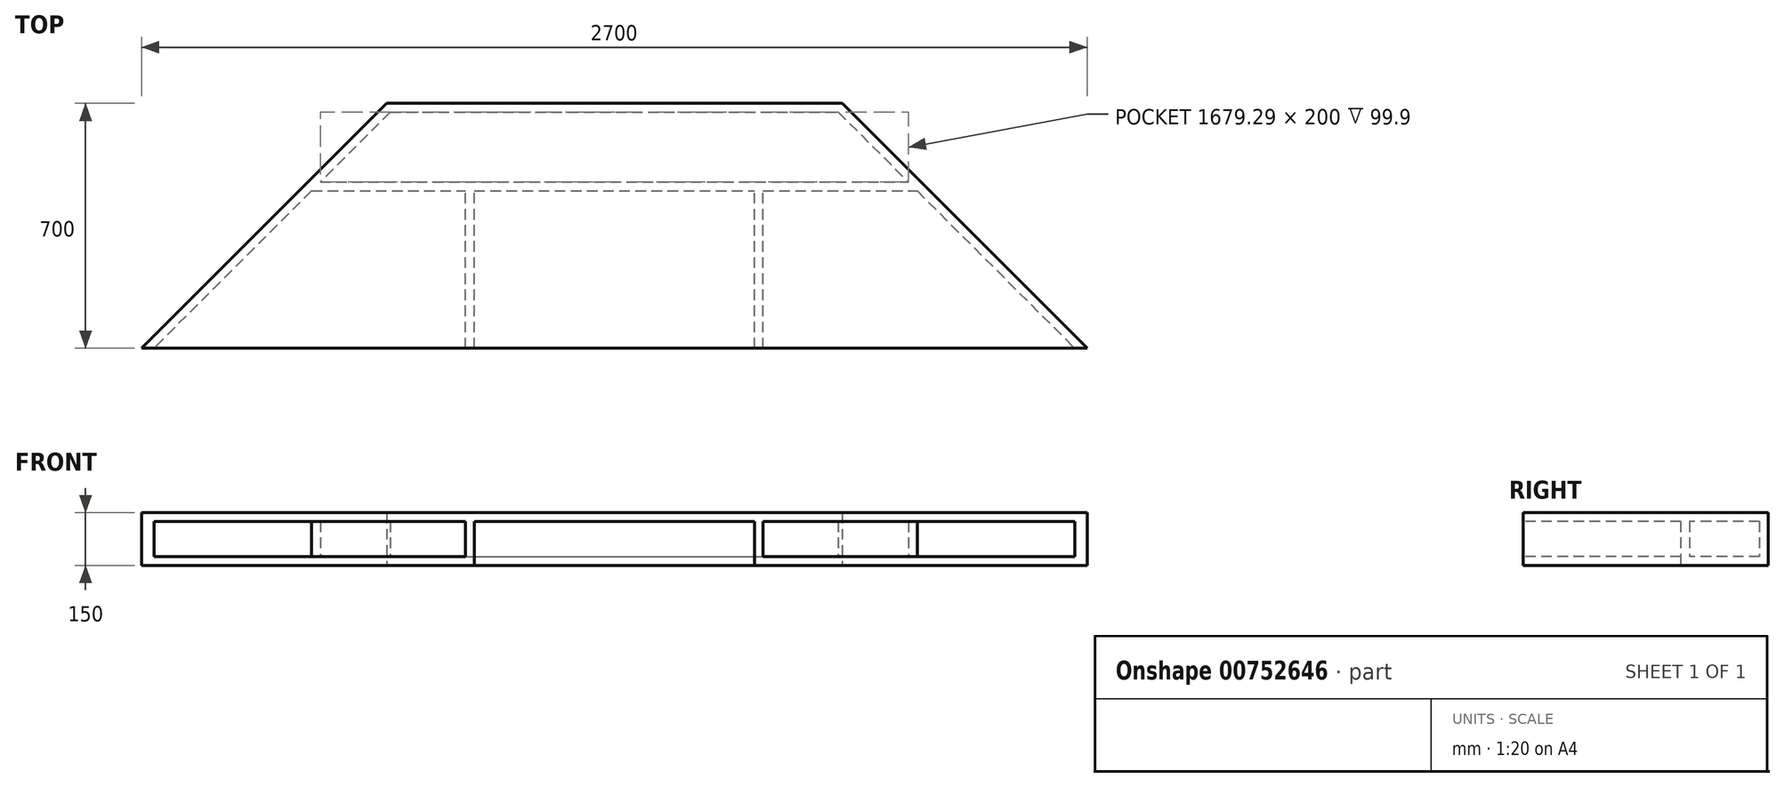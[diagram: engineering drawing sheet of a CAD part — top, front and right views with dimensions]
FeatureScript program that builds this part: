
annotation { "Feature Type Name" : "Feature", "Feature Type Description" : "" }
export const myFeature = defineFeature(function(context is Context, id is Id, definition is map)
    precondition{}
    {
        {
            var Q0;
            Q0=qCreatedBy(makeId("Top.planeOp"),FACE);
            var sketch = newSketch(context, id + "F0", { "sketchPlane" : qUnion([Q0])});
            skLineSegment(sketch, "E0", {"start": v(-650, 0) * mm, "end": v(650, 0) * mm});
            skLineSegment(sketch, "E1", {"start": v(0, 0) * mm, "end": v(0, -700) * mm});
            skLineSegment(sketch, "E2", {"start": v(0, -700) * mm, "end": v(1350, -700) * mm});
            skLineSegment(sketch, "E3", {"start": v(0, -700) * mm, "end": v(-1350, -700) * mm});
            skLineSegment(sketch, "E4", {"start": v(-1350, -700) * mm, "end": v(-650, 0) * mm});
            skLineSegment(sketch, "E5", {"start": v(650, 0) * mm, "end": v(1350, -700) * mm});
            skLineSegment(sketch, "E6", {"start": v(-900, -250) * mm, "end": v(900, -250) * mm});
            skLineSegment(sketch, "E7", {"start": v(400, -700) * mm, "end": v(400, -250) * mm});
            skLineSegment(sketch, "E8", {"start": v(-400, -700) * mm, "end": v(-400, -250) * mm});
            skLineSegment(sketch, "E9", {"start": v(-875, -225) * mm, "end": v(875, -225) * mm});
            skLineSegment(sketch, "E10", {"start": v(-425, -700) * mm, "end": v(-425, -250) * mm});
            skLineSegment(sketch, "E11", {"start": v(425, -700) * mm, "end": v(425, -250) * mm});
            skLineSegment(sketch, "E12", {"start": v(-614.64, 0) * mm, "end": v(-1314.64, -700) * mm});
            skLineSegment(sketch, "E13", {"start": v(614.64, 0) * mm, "end": v(1314.64, -700) * mm});
            skLineSegment(sketch, "E14", {"start": v(-639.64, -25) * mm, "end": v(639.64, -25) * mm});
            skSolve(sketch);
        }
        {
            var Q0;
            {var subQ0=sQuery(id+"F0.wireOp",EDGE,"E4");var subQ1=sQuery(id+"F0.wireOp",EDGE,"E3");var subQ2=makeQuery(id+"F0.imprint","INTERSECT",VERTEX,{"derivedFrom":[subQ1,subQ0]});Q0=makeQuery(id+"F0.imprint","IMPRINT",FACE,{"disambiguationData":[TD([[makeQuery(id+"F0.imprint","IMPRINT",EDGE,{"disambiguationData":[TD([[subQ2,1.0]])],"derivedFrom":subQ1}),-1.0]])]});}
            var Q1;
            {var subQ0=sQuery(id+"F0.wireOp",EDGE,"E6");var subQ1=sQuery(id+"F0.wireOp",EDGE,"E4");var subQ2=makeQuery(id+"F0.imprint","INTERSECT",VERTEX,{"derivedFrom":[subQ1,subQ0]});Q1=makeQuery(id+"F0.imprint","IMPRINT",FACE,{"disambiguationData":[TD([[makeQuery(id+"F0.imprint","IMPRINT",EDGE,{"disambiguationData":[TD([[subQ2,-1.0]])],"derivedFrom":subQ1}),-1.0]])]});}
            var Q2;
            {var subQ1=sQuery(id+"F0.wireOp",EDGE,"E4");var subQ5=sQuery(id+"F0.wireOp",EDGE,"E0");var subQ8=makeQuery(id+"F0.imprint","INTERSECT",VERTEX,{"derivedFrom":[subQ5,subQ1]});Q2=makeQuery(id+"F0.imprint","IMPRINT",FACE,{"disambiguationData":[TD([[makeQuery(id+"F0.imprint","IMPRINT",EDGE,{"disambiguationData":[TD([[subQ8,-1.0]])],"derivedFrom":subQ5}),-1.0]])]});}
            var Q3;
            {var subQ2=sQuery(id+"F0.wireOp",EDGE,"E1");var subQ7=sQuery(id+"F0.wireOp",EDGE,"E9");var subQ8=makeQuery(id+"F0.imprint","INTERSECT",VERTEX,{"derivedFrom":[subQ2,subQ7]});Q3=makeQuery(id+"F0.imprint","IMPRINT",FACE,{"disambiguationData":[TD([[makeQuery(id+"F0.imprint","IMPRINT",EDGE,{"disambiguationData":[TD([[subQ8,-1.0]])],"derivedFrom":subQ2}),-1.0]])]});}
            var Q4;
            {var subQ0=sQuery(id+"F0.wireOp",EDGE,"E1");var subQ1=sQuery(id+"F0.wireOp",EDGE,"E0");var subQ2=makeQuery(id+"F0.imprint","INTERSECT",VERTEX,{"derivedFrom":[subQ1,subQ0]});Q4=makeQuery(id+"F0.imprint","IMPRINT",FACE,{"disambiguationData":[TD([[makeQuery(id+"F0.imprint","IMPRINT",EDGE,{"disambiguationData":[TD([[subQ2,1.0]])],"derivedFrom":subQ1}),-1.0]])]});}
            var Q5;
            {var subQ0=sQuery(id+"F0.wireOp",EDGE,"E1");var subQ1=sQuery(id+"F0.wireOp",EDGE,"E0");var subQ2=makeQuery(id+"F0.imprint","INTERSECT",VERTEX,{"derivedFrom":[subQ1,subQ0]});Q5=makeQuery(id+"F0.imprint","IMPRINT",FACE,{"disambiguationData":[TD([[makeQuery(id+"F0.imprint","IMPRINT",EDGE,{"disambiguationData":[TD([[subQ2,-1.0]])],"derivedFrom":subQ1}),-1.0]])]});}
            var Q6;
            {var subQ4=sQuery(id+"F0.wireOp",EDGE,"E9");var subQ5=sQuery(id+"F0.wireOp",EDGE,"E1");var subQ6=makeQuery(id+"F0.imprint","INTERSECT",VERTEX,{"derivedFrom":[subQ5,subQ4]});Q6=makeQuery(id+"F0.imprint","IMPRINT",FACE,{"disambiguationData":[TD([[makeQuery(id+"F0.imprint","IMPRINT",EDGE,{"disambiguationData":[TD([[subQ6,-1.0]])],"derivedFrom":subQ5}),1.0]])]});}
            var Q7;
            {var subQ0=sQuery(id+"F0.wireOp",EDGE,"E7");Q7=makeQuery(id+"F0.imprint","IMPRINT",FACE,{"disambiguationData":[TD([[makeQuery(id+"F0.imprint","IMPRINT",EDGE,{"derivedFrom":subQ0}),-1.0]])]});}
            var Q8;
            {var subQ0=sQuery(id+"F0.wireOp",EDGE,"E8");Q8=makeQuery(id+"F0.imprint","IMPRINT",FACE,{"disambiguationData":[TD([[makeQuery(id+"F0.imprint","IMPRINT",EDGE,{"derivedFrom":subQ0}),1.0]])]});}
            var Q9;
            {var subQ1=sQuery(id+"F0.wireOp",EDGE,"E0");var subQ5=sQuery(id+"F0.wireOp",EDGE,"E5");var subQ8=makeQuery(id+"F0.imprint","INTERSECT",VERTEX,{"derivedFrom":[subQ1,subQ5]});Q9=makeQuery(id+"F0.imprint","IMPRINT",FACE,{"disambiguationData":[TD([[makeQuery(id+"F0.imprint","IMPRINT",EDGE,{"disambiguationData":[TD([[subQ8,1.0]])],"derivedFrom":subQ1}),-1.0]])]});}
            var Q10;
            {var subQ0=sQuery(id+"F0.wireOp",EDGE,"E5");var subQ1=sQuery(id+"F0.wireOp",EDGE,"E2");var subQ2=makeQuery(id+"F0.imprint","INTERSECT",VERTEX,{"derivedFrom":[subQ1,subQ0]});Q10=makeQuery(id+"F0.imprint","IMPRINT",FACE,{"disambiguationData":[TD([[makeQuery(id+"F0.imprint","IMPRINT",EDGE,{"disambiguationData":[TD([[subQ2,1.0]])],"derivedFrom":subQ1}),1.0]])]});}
            var Q11;
            {var subQ0=sQuery(id+"F0.wireOp",EDGE,"E6");var subQ1=sQuery(id+"F0.wireOp",EDGE,"E5");var subQ2=makeQuery(id+"F0.imprint","INTERSECT",VERTEX,{"derivedFrom":[subQ1,subQ0]});Q11=makeQuery(id+"F0.imprint","IMPRINT",FACE,{"disambiguationData":[TD([[makeQuery(id+"F0.imprint","IMPRINT",EDGE,{"disambiguationData":[TD([[subQ2,1.0]])],"derivedFrom":subQ1}),-1.0]])]});}
            extrude(context, id + "F1", {"entities" : qUnion([Q0, Q1, Q2, Q3, Q4, Q5, Q6, Q7, Q8, Q9, Q10, Q11]), "depth" : 125 * mm, "offsetDistance" : 25 * mm});
        }
        {
            var Q0;
            {var subQ0=sQuery(id+"F0.wireOp",EDGE,"E11");Q0=makeQuery(id+"F0.imprint","IMPRINT",FACE,{"disambiguationData":[TD([[makeQuery(id+"F0.imprint","IMPRINT",EDGE,{"derivedFrom":subQ0}),-1.0]])]});}
            var Q1;
            {var subQ4=sQuery(id+"F0.wireOp",EDGE,"E9");var subQ5=sQuery(id+"F0.wireOp",EDGE,"E1");var subQ6=makeQuery(id+"F0.imprint","INTERSECT",VERTEX,{"derivedFrom":[subQ5,subQ4]});Q1=makeQuery(id+"F0.imprint","IMPRINT",FACE,{"disambiguationData":[TD([[makeQuery(id+"F0.imprint","IMPRINT",EDGE,{"disambiguationData":[TD([[subQ6,-1.0]])],"derivedFrom":subQ5}),1.0]])]});}
            var Q2;
            {var subQ0=sQuery(id+"F0.wireOp",EDGE,"E6");var subQ1=sQuery(id+"F0.wireOp",EDGE,"E5");var subQ2=makeQuery(id+"F0.imprint","INTERSECT",VERTEX,{"derivedFrom":[subQ1,subQ0]});Q2=makeQuery(id+"F0.imprint","IMPRINT",FACE,{"disambiguationData":[TD([[makeQuery(id+"F0.imprint","IMPRINT",EDGE,{"disambiguationData":[TD([[subQ2,1.0]])],"derivedFrom":subQ1}),-1.0]])]});}
            var Q3;
            {var subQ0=sQuery(id+"F0.wireOp",EDGE,"E5");var subQ1=sQuery(id+"F0.wireOp",EDGE,"E2");var subQ2=makeQuery(id+"F0.imprint","INTERSECT",VERTEX,{"derivedFrom":[subQ1,subQ0]});Q3=makeQuery(id+"F0.imprint","IMPRINT",FACE,{"disambiguationData":[TD([[makeQuery(id+"F0.imprint","IMPRINT",EDGE,{"disambiguationData":[TD([[subQ2,1.0]])],"derivedFrom":subQ1}),1.0]])]});}
            var Q4;
            {var subQ1=sQuery(id+"F0.wireOp",EDGE,"E0");var subQ5=sQuery(id+"F0.wireOp",EDGE,"E5");var subQ8=makeQuery(id+"F0.imprint","INTERSECT",VERTEX,{"derivedFrom":[subQ1,subQ5]});Q4=makeQuery(id+"F0.imprint","IMPRINT",FACE,{"disambiguationData":[TD([[makeQuery(id+"F0.imprint","IMPRINT",EDGE,{"disambiguationData":[TD([[subQ8,1.0]])],"derivedFrom":subQ1}),-1.0]])]});}
            var Q5;
            {var subQ0=sQuery(id+"F0.wireOp",EDGE,"E14");var subQ1=sQuery(id+"F0.wireOp",EDGE,"E1");var subQ2=makeQuery(id+"F0.imprint","INTERSECT",VERTEX,{"derivedFrom":[subQ1,subQ0]});Q5=makeQuery(id+"F0.imprint","IMPRINT",FACE,{"disambiguationData":[TD([[makeQuery(id+"F0.imprint","IMPRINT",EDGE,{"disambiguationData":[TD([[subQ2,-1.0]])],"derivedFrom":subQ1}),1.0]])]});}
            var Q6;
            {var subQ0=sQuery(id+"F0.wireOp",EDGE,"E7");Q6=makeQuery(id+"F0.imprint","IMPRINT",FACE,{"disambiguationData":[TD([[makeQuery(id+"F0.imprint","IMPRINT",EDGE,{"derivedFrom":subQ0}),-1.0]])]});}
            var Q7;
            {var subQ0=sQuery(id+"F0.wireOp",EDGE,"E1");var subQ1=sQuery(id+"F0.wireOp",EDGE,"E0");var subQ2=makeQuery(id+"F0.imprint","INTERSECT",VERTEX,{"derivedFrom":[subQ1,subQ0]});Q7=makeQuery(id+"F0.imprint","IMPRINT",FACE,{"disambiguationData":[TD([[makeQuery(id+"F0.imprint","IMPRINT",EDGE,{"disambiguationData":[TD([[subQ2,-1.0]])],"derivedFrom":subQ1}),-1.0]])]});}
            var Q8;
            {var subQ0=sQuery(id+"F0.wireOp",EDGE,"E1");var subQ1=sQuery(id+"F0.wireOp",EDGE,"E0");var subQ2=makeQuery(id+"F0.imprint","INTERSECT",VERTEX,{"derivedFrom":[subQ1,subQ0]});Q8=makeQuery(id+"F0.imprint","IMPRINT",FACE,{"disambiguationData":[TD([[makeQuery(id+"F0.imprint","IMPRINT",EDGE,{"disambiguationData":[TD([[subQ2,1.0]])],"derivedFrom":subQ1}),-1.0]])]});}
            var Q9;
            {var subQ0=sQuery(id+"F0.wireOp",EDGE,"E14");var subQ1=sQuery(id+"F0.wireOp",EDGE,"E1");var subQ2=makeQuery(id+"F0.imprint","INTERSECT",VERTEX,{"derivedFrom":[subQ1,subQ0]});Q9=makeQuery(id+"F0.imprint","IMPRINT",FACE,{"disambiguationData":[TD([[makeQuery(id+"F0.imprint","IMPRINT",EDGE,{"disambiguationData":[TD([[subQ2,-1.0]])],"derivedFrom":subQ1}),-1.0]])]});}
            var Q10;
            {var subQ2=sQuery(id+"F0.wireOp",EDGE,"E1");var subQ7=sQuery(id+"F0.wireOp",EDGE,"E9");var subQ8=makeQuery(id+"F0.imprint","INTERSECT",VERTEX,{"derivedFrom":[subQ2,subQ7]});Q10=makeQuery(id+"F0.imprint","IMPRINT",FACE,{"disambiguationData":[TD([[makeQuery(id+"F0.imprint","IMPRINT",EDGE,{"disambiguationData":[TD([[subQ8,-1.0]])],"derivedFrom":subQ2}),-1.0]])]});}
            var Q11;
            {var subQ0=sQuery(id+"F0.wireOp",EDGE,"E8");Q11=makeQuery(id+"F0.imprint","IMPRINT",FACE,{"disambiguationData":[TD([[makeQuery(id+"F0.imprint","IMPRINT",EDGE,{"derivedFrom":subQ0}),1.0]])]});}
            var Q12;
            {var subQ0=sQuery(id+"F0.wireOp",EDGE,"E10");Q12=makeQuery(id+"F0.imprint","IMPRINT",FACE,{"disambiguationData":[TD([[makeQuery(id+"F0.imprint","IMPRINT",EDGE,{"derivedFrom":subQ0}),1.0]])]});}
            var Q13;
            {var subQ1=sQuery(id+"F0.wireOp",EDGE,"E4");var subQ5=sQuery(id+"F0.wireOp",EDGE,"E0");var subQ8=makeQuery(id+"F0.imprint","INTERSECT",VERTEX,{"derivedFrom":[subQ5,subQ1]});Q13=makeQuery(id+"F0.imprint","IMPRINT",FACE,{"disambiguationData":[TD([[makeQuery(id+"F0.imprint","IMPRINT",EDGE,{"disambiguationData":[TD([[subQ8,-1.0]])],"derivedFrom":subQ5}),-1.0]])]});}
            var Q14;
            {var subQ0=sQuery(id+"F0.wireOp",EDGE,"E6");var subQ1=sQuery(id+"F0.wireOp",EDGE,"E4");var subQ2=makeQuery(id+"F0.imprint","INTERSECT",VERTEX,{"derivedFrom":[subQ1,subQ0]});Q14=makeQuery(id+"F0.imprint","IMPRINT",FACE,{"disambiguationData":[TD([[makeQuery(id+"F0.imprint","IMPRINT",EDGE,{"disambiguationData":[TD([[subQ2,-1.0]])],"derivedFrom":subQ1}),-1.0]])]});}
            var Q15;
            {var subQ0=sQuery(id+"F0.wireOp",EDGE,"E4");var subQ1=sQuery(id+"F0.wireOp",EDGE,"E3");var subQ2=makeQuery(id+"F0.imprint","INTERSECT",VERTEX,{"derivedFrom":[subQ1,subQ0]});Q15=makeQuery(id+"F0.imprint","IMPRINT",FACE,{"disambiguationData":[TD([[makeQuery(id+"F0.imprint","IMPRINT",EDGE,{"disambiguationData":[TD([[subQ2,1.0]])],"derivedFrom":subQ1}),-1.0]])]});}
            extrude(context, id + "F2", {"entities" : qUnion([Q0, Q1, Q2, Q3, Q4, Q5, Q6, Q7, Q8, Q9, Q10, Q11, Q12, Q13, Q14, Q15]), "operationType" : NewBodyOperationType.ADD, "depth" : 25 * mm, "offsetDistance" : 25 * mm});
        }
        {
            var Q0;
            Q0 = qSketchRegion(id + "F0", true);
            var Q1;
            {var subQ0=sQuery(id+"F0.wireOp",EDGE,"E14");var subQ1=sQuery(id+"F0.wireOp",EDGE,"E1");var subQ2=makeQuery(id+"F0.imprint","INTERSECT",VERTEX,{"derivedFrom":[subQ1,subQ0]});Q1=makeQuery(id+"F0.imprint","IMPRINT",FACE,{"disambiguationData":[TD([[makeQuery(id+"F0.imprint","IMPRINT",EDGE,{"disambiguationData":[TD([[subQ2,-1.0]])],"derivedFrom":subQ1}),1.0]])]});}
            var Q2;
            {var subQ0=sQuery(id+"F0.wireOp",EDGE,"E14");var subQ1=sQuery(id+"F0.wireOp",EDGE,"E1");var subQ2=makeQuery(id+"F0.imprint","INTERSECT",VERTEX,{"derivedFrom":[subQ1,subQ0]});Q2=makeQuery(id+"F0.imprint","IMPRINT",FACE,{"disambiguationData":[TD([[makeQuery(id+"F0.imprint","IMPRINT",EDGE,{"disambiguationData":[TD([[subQ2,-1.0]])],"derivedFrom":subQ1}),-1.0]])]});}
            var Q3;
            {var subQ4=sQuery(id+"F0.wireOp",EDGE,"E9");var subQ5=sQuery(id+"F0.wireOp",EDGE,"E1");var subQ6=makeQuery(id+"F0.imprint","INTERSECT",VERTEX,{"derivedFrom":[subQ5,subQ4]});Q3=makeQuery(id+"F0.imprint","IMPRINT",FACE,{"disambiguationData":[TD([[makeQuery(id+"F0.imprint","IMPRINT",EDGE,{"disambiguationData":[TD([[subQ6,-1.0]])],"derivedFrom":subQ5}),1.0]])]});}
            var Q4;
            {var subQ2=sQuery(id+"F0.wireOp",EDGE,"E1");var subQ7=sQuery(id+"F0.wireOp",EDGE,"E9");var subQ8=makeQuery(id+"F0.imprint","INTERSECT",VERTEX,{"derivedFrom":[subQ2,subQ7]});Q4=makeQuery(id+"F0.imprint","IMPRINT",FACE,{"disambiguationData":[TD([[makeQuery(id+"F0.imprint","IMPRINT",EDGE,{"disambiguationData":[TD([[subQ8,-1.0]])],"derivedFrom":subQ2}),-1.0]])]});}
            extrude(context, id + "F3", {"entities" : qUnion([Q0, Q1, Q2, Q3, Q4]), "operationType" : NewBodyOperationType.ADD, "depth" : 150 * mm, "offsetDistance" : 25 * mm, "hasSecondDirection" : true, "secondDirectionOppositeDirection" : false, "secondDirectionDepth" : 124.9 * mm});
        }
    });
